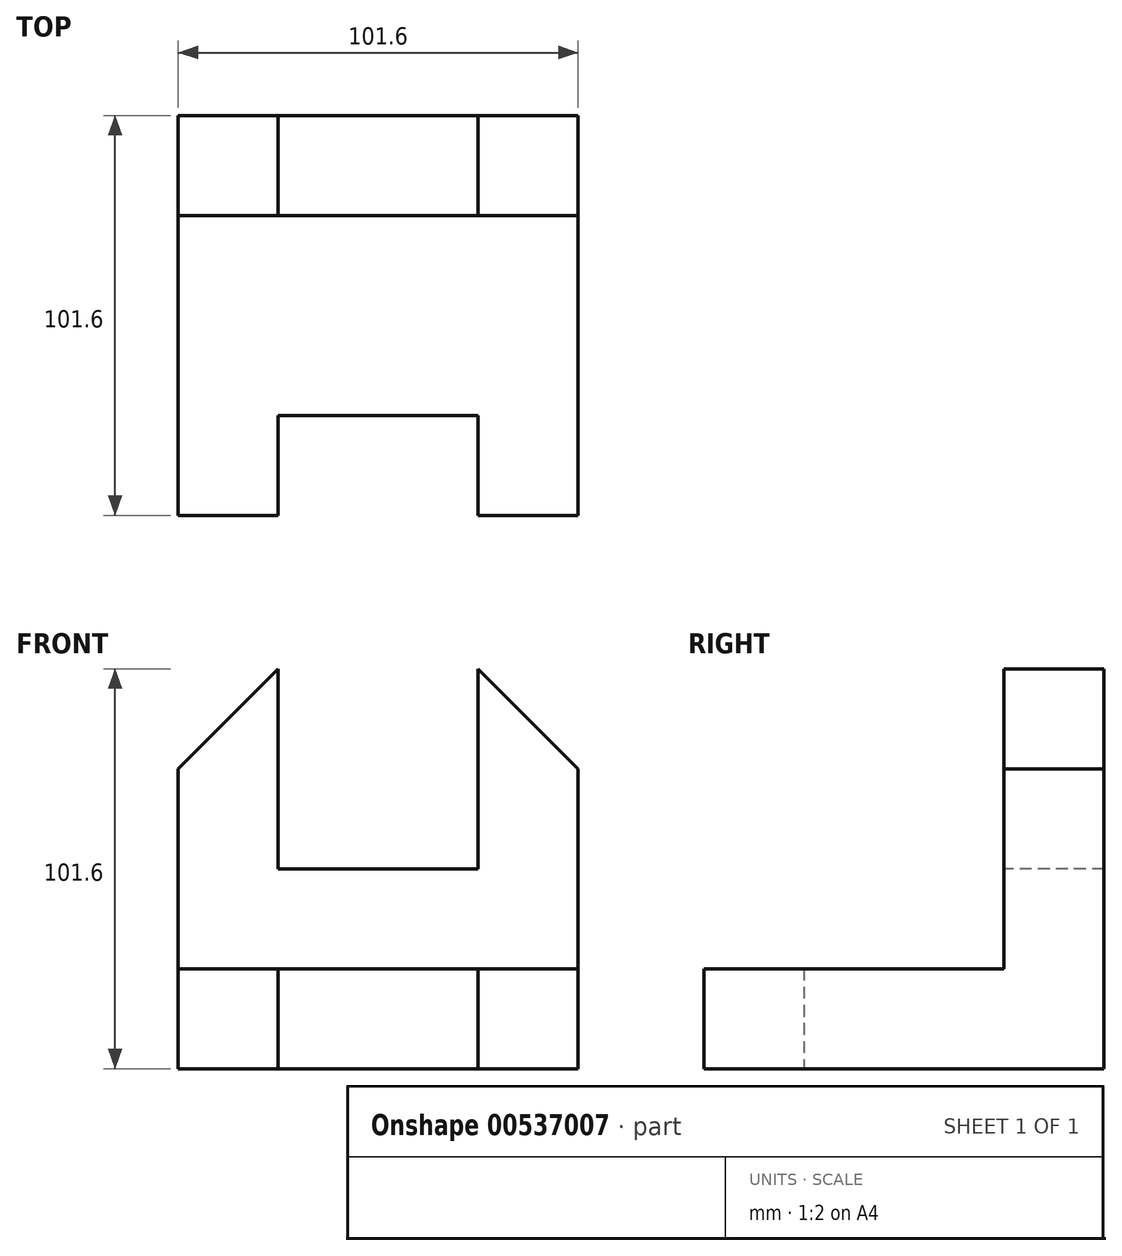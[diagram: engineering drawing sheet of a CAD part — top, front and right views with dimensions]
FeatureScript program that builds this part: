
annotation { "Feature Type Name" : "Feature", "Feature Type Description" : "" }
export const myFeature = defineFeature(function(context is Context, id is Id, definition is map)
    precondition{}
    {
        {
            var Q0;
            Q0=qCreatedBy(makeId("Top.planeOp"),FACE);
            var sketch = newSketch(context, id + "F0", { "sketchPlane" : qUnion([Q0])});
            skLineSegment(sketch, "E0.bottom", {"start": v(0, 0) * mm, "end": v(101.6, 0) * mm});
            skLineSegment(sketch, "E0.top", {"start": v(0, -101.6) * mm, "end": v(101.6, -101.6) * mm});
            skLineSegment(sketch, "E0.left", {"start": v(0, 0) * mm, "end": v(0, -101.6) * mm});
            skLineSegment(sketch, "E0.right", {"start": v(101.6, 0) * mm, "end": v(101.6, -101.6) * mm});
            skSolve(sketch);
        }
        {
            var Q0;
            Q0 = qSketchRegion(id + "F0", true);
            extrude(context, id + "F1", {"entities" : qUnion([Q0]), "depth" : 101.6 * mm, "offsetDistance" : 25.4 * mm});
        }
        {
            var Q0;
            Q0=makeQuery(id+"F1.opExtrude","SWEPT_FACE",FACE,{"disambiguationData":[OSD([sQuery(id+"F0.wireOp",EDGE,"E0.top")])]});
            var sketch = newSketch(context, id + "F2", { "sketchPlane" : qUnion([Q0])});
            skLineSegment(sketch, "E1.bottom", {"start": v(0, 101.6) * mm, "end": v(101.6, 101.6) * mm});
            skLineSegment(sketch, "E1.top", {"start": v(0, 25.4) * mm, "end": v(101.6, 25.4) * mm});
            skLineSegment(sketch, "E1.left", {"start": v(0, 101.6) * mm, "end": v(0, 25.4) * mm});
            skLineSegment(sketch, "E1.right", {"start": v(101.6, 101.6) * mm, "end": v(101.6, 25.4) * mm});
            skSolve(sketch);
        }
        {
            var Q0;
            Q0 = qSketchRegion(id + "F2", true);
            extrude(context, id + "F3", {"entities" : qUnion([Q0]), "operationType" : NewBodyOperationType.REMOVE, "oppositeDirection" : true, "depth" : 76.2 * mm, "offsetDistance" : 25.4 * mm});
        }
        {
            var Q0;
            Q0=makeQuery(id+"F1.opExtrude","SWEPT_FACE",FACE,{"disambiguationData":[OSD([sQuery(id+"F0.wireOp",EDGE,"E0.top")])]});
            var sketch = newSketch(context, id + "F4", { "sketchPlane" : qUnion([Q0])});
            skLineSegment(sketch, "E2.bottom", {"start": v(0, 25.4) * mm, "end": v(25.4, 25.4) * mm});
            skLineSegment(sketch, "E2.top", {"start": v(0, 0) * mm, "end": v(25.4, 0) * mm});
            skLineSegment(sketch, "E2.left", {"start": v(0, 25.4) * mm, "end": v(0, 0) * mm});
            skLineSegment(sketch, "E2.right", {"start": v(25.4, 25.4) * mm, "end": v(25.4, 0) * mm});
            skLineSegment(sketch, "E3.bottom", {"start": v(101.6, 25.4) * mm, "end": v(76.2, 25.4) * mm});
            skLineSegment(sketch, "E3.top", {"start": v(101.6, 0) * mm, "end": v(76.2, 0) * mm});
            skLineSegment(sketch, "E3.left", {"start": v(101.6, 25.4) * mm, "end": v(101.6, 0) * mm});
            skLineSegment(sketch, "E3.right", {"start": v(76.2, 25.4) * mm, "end": v(76.2, 0) * mm});
            skLineSegment(sketch, "E4", {"start": v(76.2, 25.4) * mm, "end": v(25.4, 25.4) * mm});
            skLineSegment(sketch, "E5", {"start": v(76.2, 0) * mm, "end": v(25.4, 0) * mm});
            skSolve(sketch);
        }
        {
            var Q0;
            Q0=makeQuery(id+"F4.imprint","IMPRINT",FACE,{"disambiguationData":[TD([[makeQuery(id+"F4.imprint","IMPRINT",EDGE,{"derivedFrom":sQuery(id+"F4.wireOp",EDGE,"E2.right")}),1.0]])]});
            extrude(context, id + "F5", {"entities" : qUnion([Q0]), "operationType" : NewBodyOperationType.REMOVE, "oppositeDirection" : true, "depth" : 25.4 * mm, "offsetDistance" : 25.4 * mm});
        }
        {
            var Q0;
            Q0=makeQuery(id+"F3.boolean.opBoolean","COPY",FACE,{"derivedFrom":makeQuery(id+"F3.opExtrude","CAP_FACE",FACE,{"disambiguationData":[OSD([sQuery(id+"F2.wireOp",EDGE,"E1.bottom"),sQuery(id+"F2.wireOp",EDGE,"E1.top"),sQuery(id+"F2.wireOp",EDGE,"E1.left"),sQuery(id+"F2.wireOp",EDGE,"E1.right")])],"isStart":false})});
            var sketch = newSketch(context, id + "F6", { "sketchPlane" : qUnion([Q0])});
            skLineSegment(sketch, "E6.bottom", {"start": v(0, 101.6) * mm, "end": v(25.4, 101.6) * mm});
            skLineSegment(sketch, "E6.top", {"start": v(0, 50.8) * mm, "end": v(25.4, 50.8) * mm});
            skLineSegment(sketch, "E6.left", {"start": v(0, 101.6) * mm, "end": v(0, 50.8) * mm});
            skLineSegment(sketch, "E6.right", {"start": v(25.4, 101.6) * mm, "end": v(25.4, 50.8) * mm});
            skLineSegment(sketch, "E7.bottom", {"start": v(101.6, 101.6) * mm, "end": v(76.2, 101.6) * mm});
            skLineSegment(sketch, "E7.top", {"start": v(101.6, 50.8) * mm, "end": v(76.2, 50.8) * mm});
            skLineSegment(sketch, "E7.left", {"start": v(101.6, 101.6) * mm, "end": v(101.6, 50.8) * mm});
            skLineSegment(sketch, "E7.right", {"start": v(76.2, 101.6) * mm, "end": v(76.2, 50.8) * mm});
            skLineSegment(sketch, "E8", {"start": v(76.2, 101.6) * mm, "end": v(25.4, 101.6) * mm});
            skLineSegment(sketch, "E9", {"start": v(76.2, 50.8) * mm, "end": v(25.4, 50.8) * mm});
            skSolve(sketch);
        }
        {
            var Q0;
            Q0=makeQuery(id+"F6.imprint","IMPRINT",FACE,{"disambiguationData":[TD([[makeQuery(id+"F6.imprint","IMPRINT",EDGE,{"derivedFrom":sQuery(id+"F6.wireOp",EDGE,"E6.right")}),1.0]])]});
            extrude(context, id + "F7", {"entities" : qUnion([Q0]), "operationType" : NewBodyOperationType.REMOVE, "oppositeDirection" : true, "depth" : 25.4 * mm, "offsetDistance" : 25.4 * mm});
        }
        {
            var Q0;
            Q0=makeQuery(id+"F3.boolean.opBoolean","COPY",FACE,{"derivedFrom":makeQuery(id+"F3.opExtrude","CAP_FACE",FACE,{"disambiguationData":[OSD([sQuery(id+"F2.wireOp",EDGE,"E1.bottom"),sQuery(id+"F2.wireOp",EDGE,"E1.top"),sQuery(id+"F2.wireOp",EDGE,"E1.left"),sQuery(id+"F2.wireOp",EDGE,"E1.right")])],"isStart":false})});
            var sketch = newSketch(context, id + "F8", { "sketchPlane" : qUnion([Q0])});
            skLineSegment(sketch, "E10.bottom", {"start": v(0, 101.6) * mm, "end": v(25.4, 101.6) * mm});
            skLineSegment(sketch, "E10.top", {"start": v(0, 76.2) * mm, "end": v(25.4, 76.2) * mm});
            skLineSegment(sketch, "E10.left", {"start": v(0, 101.6) * mm, "end": v(0, 76.2) * mm});
            skLineSegment(sketch, "E10.right", {"start": v(25.4, 101.6) * mm, "end": v(25.4, 76.2) * mm});
            skLineSegment(sketch, "E11.bottom", {"start": v(101.6, 101.6) * mm, "end": v(76.2, 101.6) * mm});
            skLineSegment(sketch, "E11.top", {"start": v(101.6, 76.2) * mm, "end": v(76.2, 76.2) * mm});
            skLineSegment(sketch, "E11.left", {"start": v(101.6, 101.6) * mm, "end": v(101.6, 76.2) * mm});
            skLineSegment(sketch, "E11.right", {"start": v(76.2, 101.6) * mm, "end": v(76.2, 76.2) * mm});
            skLineSegment(sketch, "E12", {"start": v(25.4, 101.6) * mm, "end": v(0, 76.2) * mm});
            skLineSegment(sketch, "E13", {"start": v(76.2, 101.6) * mm, "end": v(101.6, 76.2) * mm});
            skSolve(sketch);
        }
        {
            var Q0;
            Q0=makeQuery(id+"F8.imprint","IMPRINT",FACE,{"disambiguationData":[TD([[makeQuery(id+"F8.imprint","IMPRINT",EDGE,{"derivedFrom":sQuery(id+"F8.wireOp",EDGE,"E10.bottom")}),-1.0]])]});
            var Q1;
            Q1=makeQuery(id+"F8.imprint","IMPRINT",FACE,{"disambiguationData":[TD([[makeQuery(id+"F8.imprint","IMPRINT",EDGE,{"derivedFrom":sQuery(id+"F8.wireOp",EDGE,"E11.bottom")}),-1.0]])]});
            extrude(context, id + "F9", {"entities" : qUnion([Q0, Q1]), "operationType" : NewBodyOperationType.REMOVE, "oppositeDirection" : true, "depth" : 25.4 * mm, "offsetDistance" : 25.4 * mm});
        }
    });
